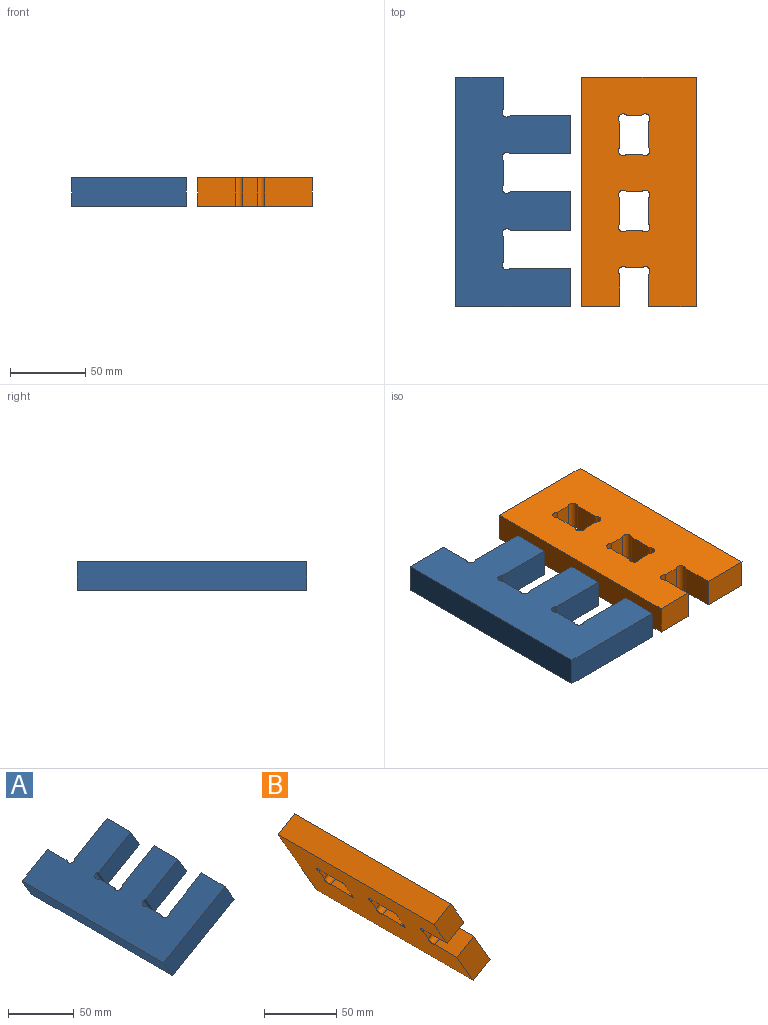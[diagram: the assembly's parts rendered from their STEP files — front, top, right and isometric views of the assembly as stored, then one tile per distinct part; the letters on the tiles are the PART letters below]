
ASSEMBLY  parts=2 mates=3
PART A: 21 faces, bbox 75.5x152.4x54.6 mm
  f0: plane 152.4x65.99mm, normal (-0.5,0,0.87), area 8197mm2, adj f2,f3,f4,f5,f6,f7,f8,f9
  f1: plane 152.4x65.99mm, normal (0.5,0,-0.87), area 8197mm2, adj f2,f3,f4,f5,f6,f7,f8,f9
  f2: plane 44.13x36.48mm, normal (0,1,0), area 761.2mm2, adj f0,f1,f11,f20
  f3: plane 20.91x16.5mm, normal (0.87,0,0.5), area 398.3mm2, adj f0,f1,f14,f20
  f4: plane 44.13x36.48mm, normal (0,1,0), area 761.2mm2, adj f0,f1,f10,f19
  f5: plane 16.5x16.42mm, normal (0.87,0,0.5), area 312.8mm2, adj f0,f1,f18,f19
  f6: plane 44.13x36.48mm, normal (0,-1,0), area 761.2mm2, adj f0,f1,f11,f18
  f7: plane 44.13x36.48mm, normal (0,1,0), area 761.2mm2, adj f0,f1,f15,f17
  f8: plane 16.5x16.42mm, normal (0.87,0,0.5), area 312.8mm2, adj f0,f1,f16,f17
  f9: plane 44.13x36.48mm, normal (0,-1,0), area 761.2mm2, adj f0,f1,f10,f16
  f10: plane 25.4x16.5mm, normal (0.87,0,0.5), area 483.9mm2, adj f0,f1,f4,f9
  f11: plane 25.4x16.5mm, normal (0.87,0,0.5), area 483.9mm2, adj f0,f1,f2,f6
  f12: plane 75.52x54.6mm, normal (0,-1,0), area 1451.6mm2, adj f0,f1,f13,f15
  f13: plane 152.4x16.5mm, normal (-0.87,0,-0.5), area 2903.2mm2, adj f0,f1,f12,f14
  f14: plane 37.02x32.37mm, normal (0,1,0), area 604.8mm2, adj f0,f1,f3,f13
  f15: plane 25.4x16.5mm, normal (0.87,0,0.5), area 483.9mm2, adj f0,f1,f7,f12
  f16: cylinder r=3.17mm len=19.21mm, axis (-0.5,0,0.87), area 190mm2, adj f0,f1,f8,f9
  f17: cylinder r=3.17mm len=19.21mm, axis (-0.5,0,0.87), area 190mm2, adj f0,f1,f7,f8
  f18: cylinder r=3.17mm len=19.21mm, axis (-0.5,0,0.87), area 190mm2, adj f0,f1,f5,f6
  f19: cylinder r=3.17mm len=19.21mm, axis (-0.5,0,0.87), area 190mm2, adj f0,f1,f4,f5
  f20: cylinder r=3.17mm len=19.21mm, axis (-0.5,0,0.87), area 190mm2, adj f0,f1,f2,f3
PART B: 28 faces, bbox 54.6x152.4x75.5 mm
  f0: plane 16.93x16.5mm, normal (0.5,0,-0.87), area 322.5mm2, adj f12,f13,f24,f26
  f1: plane 16.93x16.5mm, normal (-0.5,0,0.87), area 322.5mm2, adj f12,f13,f25,f27
  f2: plane 21.53x18.25mm, normal (0,-1,0), area 191.8mm2, adj f12,f13,f26,f27
  f3: plane 21.53x18.25mm, normal (0,1,0), area 191.8mm2, adj f12,f13,f24,f25
  f4: plane 21.53x18.25mm, normal (0,1,0), area 191.8mm2, adj f12,f13,f20,f23
  f5: plane 21.53x18.25mm, normal (0,-1,0), area 191.8mm2, adj f12,f13,f21,f22
  f6: plane 16.93x16.5mm, normal (-0.5,0,0.87), area 322.5mm2, adj f12,f13,f22,f23
  f7: plane 16.93x16.5mm, normal (0.5,0,-0.87), area 322.5mm2, adj f12,f13,f20,f21
  f8: plane 21.53x18.25mm, normal (0,-1,0), area 191.8mm2, adj f12,f13,f18,f19
  f9: plane 21.16x16.5mm, normal (-0.5,0,0.87), area 403.2mm2, adj f11,f12,f13,f19
  f10: plane 21.16x16.5mm, normal (0.5,0,-0.87), area 403.2mm2, adj f12,f13,f14,f18
  f11: plane 37.02x32.37mm, normal (0,-1,0), area 604.8mm2, adj f9,f12,f13,f15
  f12: plane 152.4x65.99mm, normal (-0.87,0,-0.5), area 10079.5mm2, adj f0,f1,f2,f3,f4,f5,f6,f7
  f13: plane 152.4x65.99mm, normal (0.87,0,0.5), area 10079.5mm2, adj f0,f1,f2,f3,f4,f5,f6,f7
  f14: plane 31.52x29.2mm, normal (0,-1,0), area 483.9mm2, adj f10,f12,f13,f17
  f15: plane 152.4x16.5mm, normal (0.5,0,-0.87), area 2903.2mm2, adj f11,f12,f13,f16
  f16: plane 75.52x54.6mm, normal (0,1,0), area 1451.6mm2, adj f12,f13,f15,f17
  f17: plane 152.4x16.5mm, normal (-0.5,0,0.87), area 2903.2mm2, adj f12,f13,f14,f16
  f18: cylinder r=3.17mm len=19.21mm, axis (0.87,0,0.5), area 190mm2, adj f8,f10,f12,f13
  f19: cylinder r=3.17mm len=19.21mm, axis (0.87,0,0.5), area 190mm2, adj f8,f9,f12,f13
  f20: cylinder r=3.17mm len=19.21mm, axis (0.87,0,0.5), area 190mm2, adj f4,f7,f12,f13
  f21: cylinder r=3.17mm len=19.21mm, axis (0.87,0,0.5), area 190mm2, adj f5,f7,f12,f13
  f22: cylinder r=3.17mm len=19.21mm, axis (0.87,0,0.5), area 190mm2, adj f5,f6,f12,f13
  f23: cylinder r=3.17mm len=19.21mm, axis (0.87,0,0.5), area 190mm2, adj f4,f6,f12,f13
  f24: cylinder r=3.17mm len=19.21mm, axis (0.87,0,0.5), area 190mm2, adj f0,f3,f12,f13
  f25: cylinder r=3.17mm len=19.21mm, axis (0.87,0,0.5), area 190mm2, adj f1,f3,f12,f13
  f26: cylinder r=3.17mm len=19.21mm, axis (0.87,0,0.5), area 190mm2, adj f0,f2,f12,f13
  f27: cylinder r=3.17mm len=19.21mm, axis (0.87,0,0.5), area 190mm2, adj f1,f2,f12,f13
PLACE A rot(axis=(0,1,0),30deg) t=(113.68,153.53,0)mm
PLACE B rot(axis=(0,-1,0),60deg) t=(128.27,153.53,81.93)mm
MATE planar A.f12 <-> B.f11  axis (0,-1,0) through (38.1,0,19.05)mm
MATE parallel B.f15 <-> A.f13  axis (1,0,0) through (160.02,76.2,9.53)mm
MATE planar B.f12 <-> A.f1  axis (0,0,-1) through (160.02,76.2,0)mm
